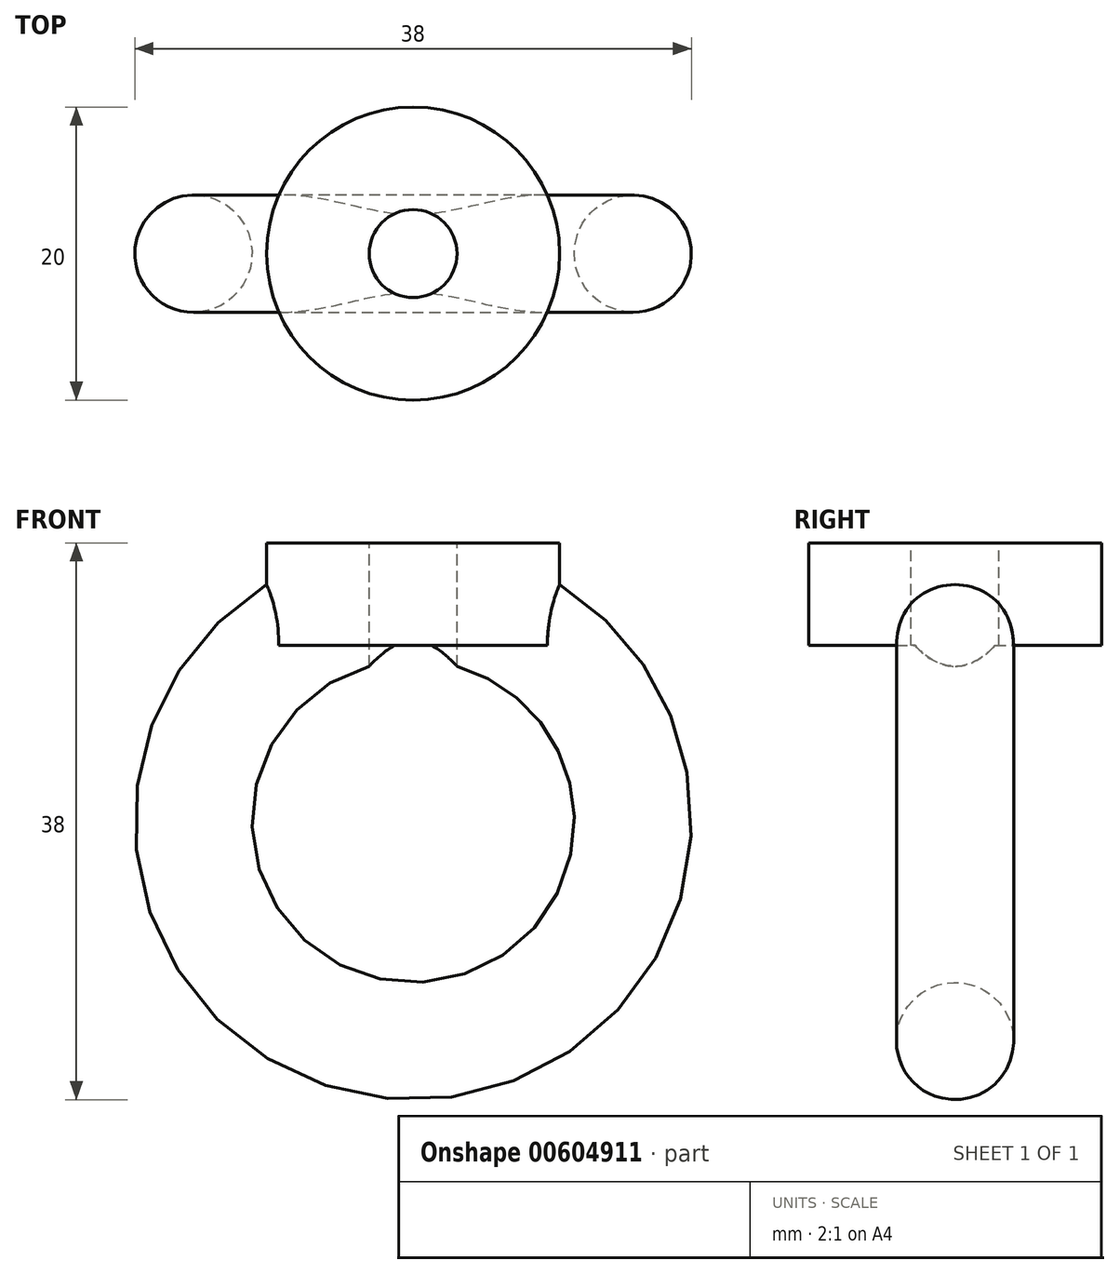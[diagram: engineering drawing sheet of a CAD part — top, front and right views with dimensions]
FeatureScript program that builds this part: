
annotation { "Feature Type Name" : "Feature", "Feature Type Description" : "" }
export const myFeature = defineFeature(function(context is Context, id is Id, definition is map)
    precondition{}
    {
        {
            var Q0;
            Q0=qCreatedBy(makeId("Top.planeOp"),FACE);
            var sketch = newSketch(context, id + "F0", { "sketchPlane" : qUnion([Q0])});
            skCircle(sketch, "E0", {"center": v(-15, 0) * mm, "radius": 4 * mm});
            skLineSegment(sketch, "E1", {"start": v(0, 0) * mm, "end": v(0, 24.86) * mm, "construction": true});
            skSolve(sketch);
        }
        {
            var Q0;
            Q0 = qSketchRegion(id + "F0", true);
            var Q1;
            Q1=sQuery(id+"F0.wireOp",EDGE,"E1");
            revolve(context, id + "F1", {"entities" : qUnion([Q0]), "axis" : qUnion([Q1]), "revolveType" : RevolveType.FULL});
        }
        {
            var Q0;
            Q0=qCreatedBy(makeId("Top.planeOp"),FACE);
            cPlane(context, id + "F2", {"entities" : qUnion([Q0]), "cplaneType" : CPlaneType.OFFSET, "offset" : 19 * mm, "width" : 150 * mm, "height" : 150 * mm});
        }
        {
            var Q0;
            Q0=qCreatedBy(id+"F2.planeOp",FACE);
            var sketch = newSketch(context, id + "F3", { "sketchPlane" : qUnion([Q0])});
            skCircle(sketch, "E2", {"center": v(0, 0) * mm, "radius": 10 * mm});
            skSolve(sketch);
        }
        {
            var Q0;
            Q0 = qSketchRegion(id + "F3", true);
            extrude(context, id + "F4", {"entities" : qUnion([Q0]), "operationType" : NewBodyOperationType.ADD, "oppositeDirection" : true, "depth" : 7 * mm, "offsetDistance" : 25 * mm});
        }
        {
            var Q0;
            Q0=makeQuery(id+"F4.opExtrude","CAP_FACE",FACE,{"disambiguationData":[OSD([sQuery(id+"F3.wireOp",EDGE,"E2")])],"isStart":true});
            var sketch = newSketch(context, id + "F5", { "sketchPlane" : qUnion([Q0])});
            skCircle(sketch, "E3", {"center": v(0, 0) * mm, "radius": 3 * mm});
            skSolve(sketch);
        }
        {
            var Q0;
            Q0 = qSketchRegion(id + "F5", true);
            extrude(context, id + "F6", {"entities" : qUnion([Q0]), "operationType" : NewBodyOperationType.REMOVE, "oppositeDirection" : true, "depth" : 10 * mm, "offsetDistance" : 25 * mm});
        }
    });
